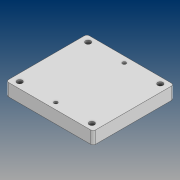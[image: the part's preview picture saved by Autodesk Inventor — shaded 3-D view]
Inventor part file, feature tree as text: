
AUTODESK INVENTOR PART (.ipt)
format: ipt  version: 2021 (Build 250183000, 183)  size: 141,824 bytes
history: native  units: mm
features: sketch x3, hole x2, mirror x2, projected_geometry x2, extrude x1, fillet x1
ambient origin geometry x8: Origin, YZ Plane, XZ Plane, XY Plane, X Axis, Y Axis, Z Axis, Center Point
bodies: Solid1 (feature_tree)
feature tree (11):
  extrude  "Extrusion1"  Depth=65.0mm
  hole  "Hole1"  [1 undecoded]
  mirror  "Mirror1"
  mirror  "Mirror2"
  fillet  "Fillet1"  Radius=10.0mm
  hole  "Hole2"  [1 undecoded]
  sketch  "Sketch1"  dims[d0=70.0mm d1=65.0mm]
  sketch  "Sketch2"  dims[d2=10.0mm d3=10.0mm d4=0.0mm d5=10.0mm]
  projected_geometry  "Projected Loop1"
  sketch  "Sketch3"  dims[d6=6.0mm d7=4.2mm d8=6.0mm d9=8.0mm d10=4.0mm d11=90.0deg d12=8.0mm d13=20.594885mm d14=2.0mm d15=2.8mm d16=6.0mm d17=8.0mm d18=4.0mm d19=90.0deg d20=8.0mm d21=20.594885mm]
  projected_geometry  "Projected Loop2"
note: 2 required parameter values undecoded (feature->parameter linkage not recoverable at this tier; creation-order binding heuristic only, values carry confidence <= 0.55)
